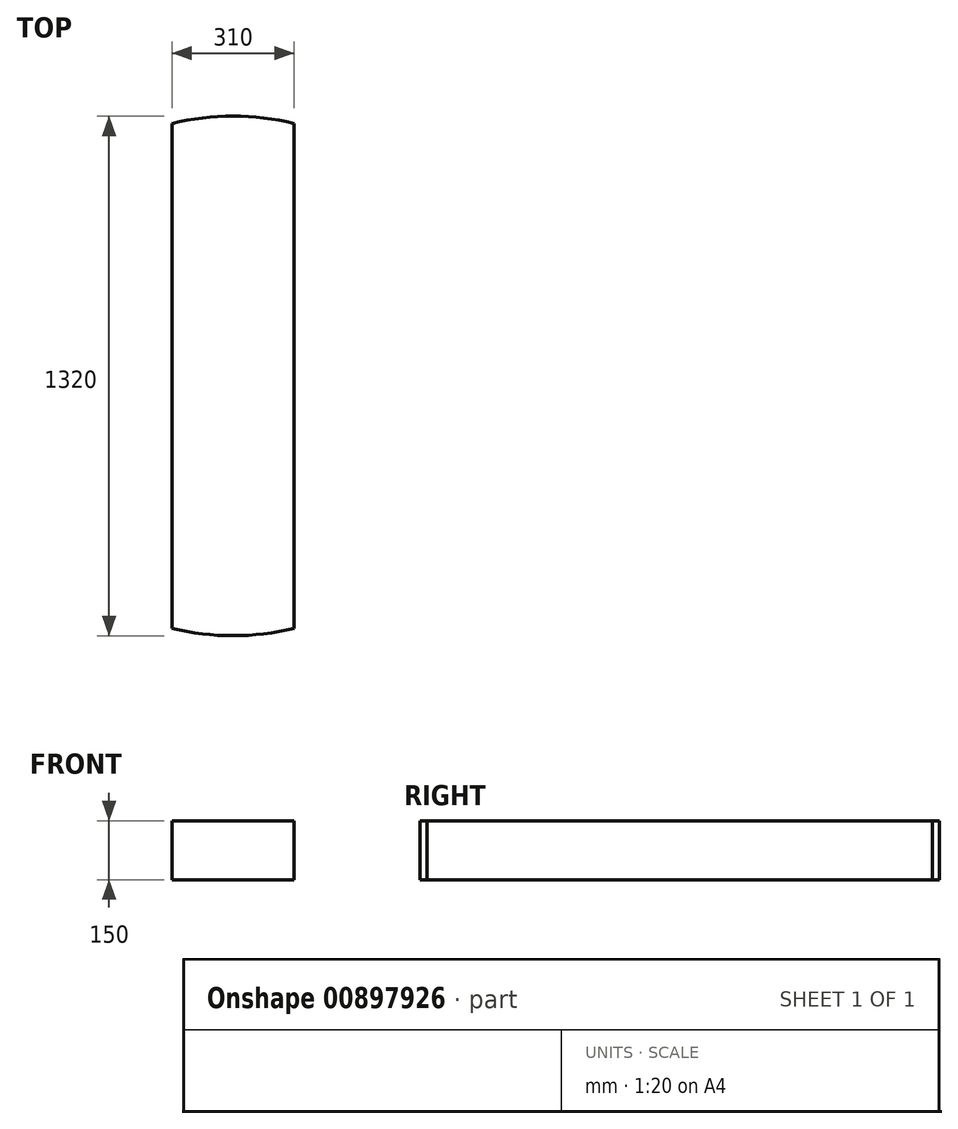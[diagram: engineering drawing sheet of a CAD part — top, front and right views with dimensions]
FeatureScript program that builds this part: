
annotation { "Feature Type Name" : "Feature", "Feature Type Description" : "" }
export const myFeature = defineFeature(function(context is Context, id is Id, definition is map)
    precondition{}
    {
        {
            var Q0;
            Q0=qCreatedBy(makeId("Top.planeOp"),FACE);
            var sketch = newSketch(context, id + "F0", { "sketchPlane" : qUnion([Q0])});
            skCircle(sketch, "E0", {"center": v(0, 0) * mm, "radius": 660 * mm});
            skLineSegment(sketch, "E1", {"start": v(155, 641.54) * mm, "end": v(155, -641.54) * mm});
            skLineSegment(sketch, "E2", {"start": v(-155, 641.54) * mm, "end": v(-155, -641.54) * mm});
            skLineSegment(sketch, "E3", {"start": v(155, 0) * mm, "end": v(-155, 0) * mm, "construction": true});
            skSolve(sketch);
        }
        {
            var Q0;
            {var subQ0=sQuery(id+"F0.wireOp",EDGE,"E1");Q0=makeQuery(id+"F0.imprint","IMPRINT",FACE,{"disambiguationData":[TD([[makeQuery(id+"F0.imprint","IMPRINT",EDGE,{"derivedFrom":subQ0}),-1.0]])]});}
            extrude(context, id + "F1", {"entities" : qUnion([Q0]), "endBound" : BoundingType.SYMMETRIC, "depth" : 150 * mm, "offsetDistance" : 25 * mm});
        }
    });
